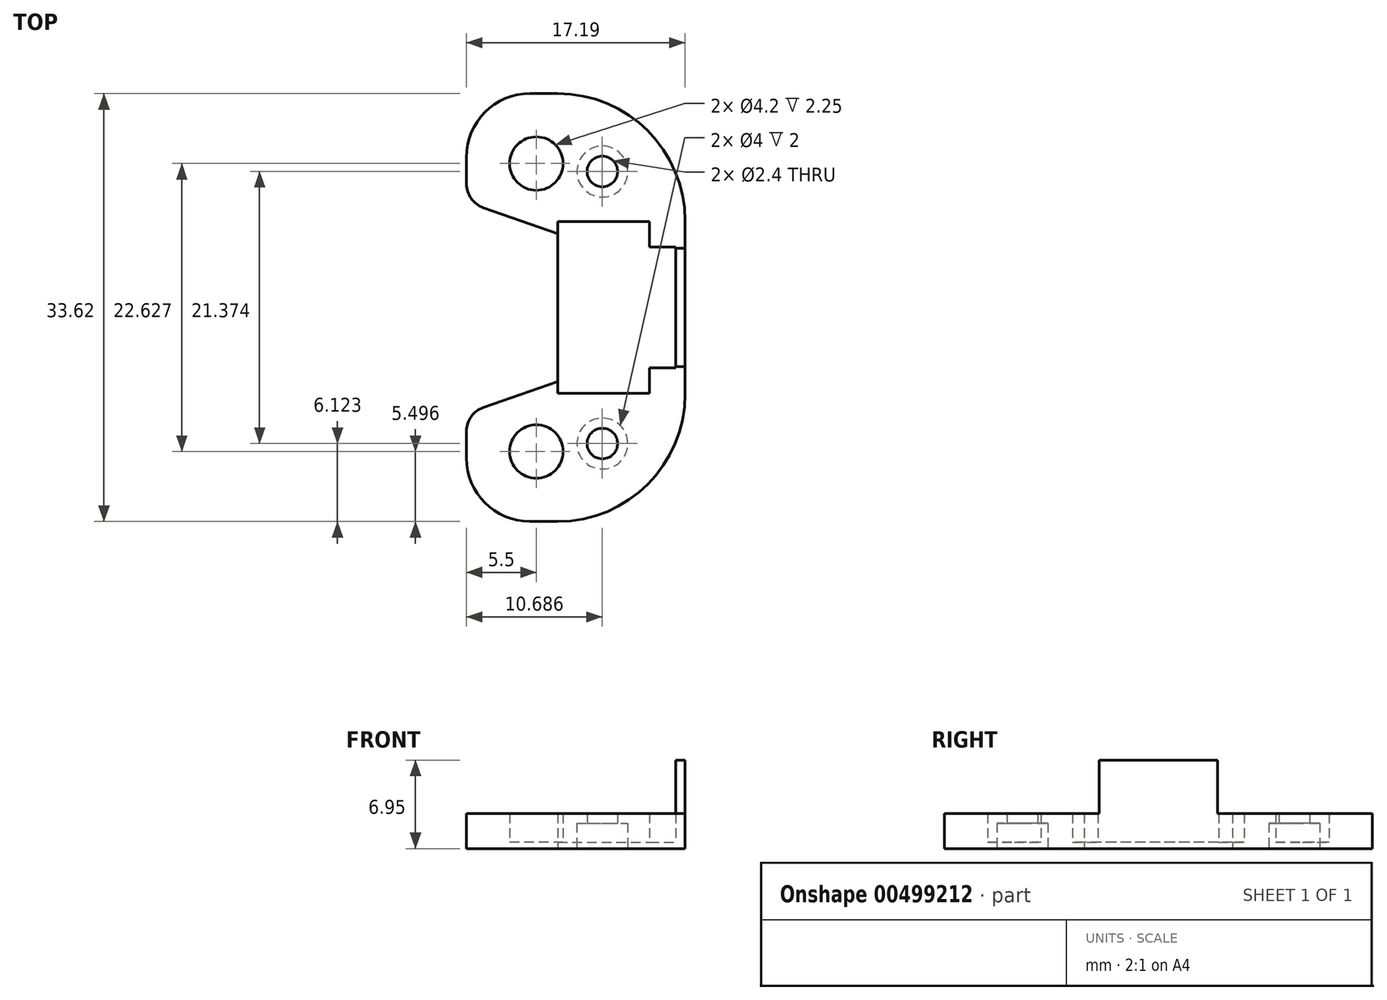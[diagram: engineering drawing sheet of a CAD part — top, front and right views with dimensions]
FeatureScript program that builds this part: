
annotation { "Feature Type Name" : "Feature", "Feature Type Description" : "" }
export const myFeature = defineFeature(function(context is Context, id is Id, definition is map)
    precondition{}
    {
        {
            var Q0;
            Q0=qCreatedBy(makeId("Top.planeOp"),FACE);
            var sketch = newSketch(context, id + "F0", { "sketchPlane" : qUnion([Q0])});
            skLineSegment(sketch, "E0.bottom", {"start": v(5.5, 16.81) * mm, "end": v(-0.5, 16.81) * mm});
            skLineSegment(sketch, "E0.top", {"start": v(5.5, 5.81) * mm, "end": v(-5.5, 5.81) * mm});
            skLineSegment(sketch, "E0.right", {"start": v(-5.5, 11.81) * mm, "end": v(-5.5, 5.81) * mm});
            skPoint(sketch, "E0.middle", {"position": v(0, 11.31) * mm});
            skLineSegment(sketch, "E1.bottom", {"start": v(5.5, -5.81) * mm, "end": v(-5.5, -5.81) * mm});
            skLineSegment(sketch, "E1.top", {"start": v(5.5, -16.81) * mm, "end": v(-0.5, -16.81) * mm});
            skLineSegment(sketch, "E1.right", {"start": v(-5.5, -5.81) * mm, "end": v(-5.5, -11.81) * mm});
            skPoint(sketch, "E1.middle", {"position": v(0, -11.31) * mm});
            skLineSegment(sketch, "E2", {"start": v(5.5, 16.81) * mm, "end": v(11.69, 16.81) * mm});
            skLineSegment(sketch, "E3", {"start": v(11.69, 16.81) * mm, "end": v(11.69, -16.81) * mm});
            skLineSegment(sketch, "E4", {"start": v(11.69, -16.81) * mm, "end": v(5.5, -16.81) * mm});
            skLineSegment(sketch, "E5", {"start": v(5.5, 5.81) * mm, "end": v(1.69, 5.81) * mm});
            skLineSegment(sketch, "E6", {"start": v(1.69, 5.81) * mm, "end": v(1.69, -5.81) * mm});
            skLineSegment(sketch, "E7", {"start": v(5.5, -5.81) * mm, "end": v(1.69, -5.81) * mm});
            skPoint(sketch, "E8", {"position": v(-11.31, 0) * mm});
            skLineSegment(sketch, "E9", {"start": v(1.69, -5.81) * mm, "end": v(-5.5, -8.31) * mm});
            skPoint(sketch, "E10.visualSharp", {"position": v(-5.5, -16.81) * mm});
            skArc(sketch, "E10.filletArc", {"start": v(-5.5, -11.81) * mm, "mid": v(-4.04, -15.35) * mm, "end": v(-0.5, -16.81) * mm});
            skPoint(sketch, "E11.visualSharp", {"position": v(-5.5, 16.81) * mm});
            skArc(sketch, "E11.filletArc", {"start": v(-0.5, 16.81) * mm, "mid": v(-4.04, 15.35) * mm, "end": v(-5.5, 11.81) * mm});
            skLineSegment(sketch, "E12", {"start": v(1.69, 5.81) * mm, "end": v(-5.5, 8.31) * mm});
            skCircle(sketch, "E13", {"center": v(0, -11.31) * mm, "radius": 2.1 * mm});
            skCircle(sketch, "E14", {"center": v(0, 11.31) * mm, "radius": 2.1 * mm});
            skSolve(sketch);
        }
        {
            var Q0;
            Q0=makeQuery(id+"F0.imprint","IMPRINT",FACE,{"disambiguationData":[TD([[makeQuery(id+"F0.imprint","IMPRINT",EDGE,{"derivedFrom":sQuery(id+"F0.wireOp",EDGE,"E0.bottom")}),1.0]])]});
            extrude(context, id + "F1", {"entities" : qUnion([Q0]), "depth" : 2.75 * mm});
        }
        {
            var Q0;
            Q0=makeQuery(id+"F1.opExtrude","SWEPT_FACE",FACE,{"disambiguationData":[OSD([sQuery(id+"F0.wireOp",EDGE,"E3")])]});
            var sketch = newSketch(context, id + "F2", { "sketchPlane" : qUnion([Q0])});
            skLineSegment(sketch, "E15.bottom", {"start": v(-6.75, 0.5) * mm, "end": v(6.75, 0.5) * mm});
            skLineSegment(sketch, "E15.top", {"start": v(-6.75, 2.75) * mm, "end": v(6.75, 2.75) * mm});
            skLineSegment(sketch, "E15.left", {"start": v(-6.75, 0.5) * mm, "end": v(-6.75, 2.75) * mm});
            skLineSegment(sketch, "E15.right", {"start": v(6.75, 0.5) * mm, "end": v(6.75, 2.75) * mm});
            skSolve(sketch);
        }
        {
            var Q0;
            Q0 = qSketchRegion(id + "F2", true);
            var Q1;
            Q1=makeQuery(id+"F1.opExtrude","SWEPT_FACE",FACE,{"disambiguationData":[OSD([sQuery(id+"F0.wireOp",EDGE,"E6")])]});
            extrude(context, id + "F3", {"entities" : qUnion([Q0]), "operationType" : NewBodyOperationType.REMOVE, "endBound" : BoundingType.UP_TO_SURFACE, "oppositeDirection" : true, "endBoundEntityFace" : qUnion([Q1]), "depth" : 25 * mm});
        }
        {
            var Q0;
            Q0=makeQuery(id+"F3.boolean.opBoolean","COPY",FACE,{"derivedFrom":makeQuery(id+"F3.opExtrude","SWEPT_FACE",FACE,{"disambiguationData":[OSD([sQuery(id+"F2.wireOp",EDGE,"E15.bottom")])]})});
            var sketch = newSketch(context, id + "F4", { "sketchPlane" : qUnion([Q0])});
            skLineSegment(sketch, "E16.bottom", {"start": v(11.69, -6.75) * mm, "end": v(8.89, -6.75) * mm});
            skLineSegment(sketch, "E16.top", {"start": v(11.69, 6.75) * mm, "end": v(8.89, 6.75) * mm});
            skLineSegment(sketch, "E16.left", {"start": v(11.69, -6.75) * mm, "end": v(11.69, -4.75) * mm});
            skLineSegment(sketch, "E16.right", {"start": v(8.89, -6.75) * mm, "end": v(8.89, -4.75) * mm});
            skLineSegment(sketch, "E17", {"start": v(8.89, -4.75) * mm, "end": v(11.69, -4.75) * mm});
            skLineSegment(sketch, "E18", {"start": v(8.89, 4.75) * mm, "end": v(11.69, 4.75) * mm});
            skLineSegment(sketch, "E19.trimOffspring", {"start": v(8.89, 4.75) * mm, "end": v(8.89, 6.75) * mm});
            skLineSegment(sketch, "E20.trimOffspring", {"start": v(11.69, 4.75) * mm, "end": v(11.69, 6.75) * mm});
            skSolve(sketch);
        }
        {
            var Q0;
            Q0 = qSketchRegion(id + "F4", true);
            var Q1;
            {var subQ0=sQuery(id+"F0.wireOp",EDGE,"E9");var subQ1=sQuery(id+"F0.wireOp",EDGE,"E3");var subQ2=sQuery(id+"F0.wireOp",EDGE,"E1.right");var subQ4=sQuery(id+"F0.wireOp",EDGE,"E4");var subQ5=sQuery(id+"F0.wireOp",EDGE,"E1.top");var subQ6=sQuery(id+"F0.wireOp",EDGE,"E10.filletArc");var subQ7=sQuery(id+"F0.wireOp",EDGE,"E13");Q1=makeQuery(id+"F3.boolean.opBoolean","SPLIT",FACE,{"disambiguationData":[TD([makeQuery(id+"F1.opExtrude","SWEPT_FACE",FACE,{"disambiguationData":[OSD([subQ2])]})])],"derivedFrom":makeQuery(id+"F1.opExtrude","CAP_FACE",FACE,{"disambiguationData":[OSD([sQuery(id+"F0.wireOp",EDGE,"E0.bottom"),sQuery(id+"F0.wireOp",EDGE,"E0.right"),subQ5,subQ2,sQuery(id+"F0.wireOp",EDGE,"E2"),subQ1,subQ4,sQuery(id+"F0.wireOp",EDGE,"E6"),subQ0,subQ6,sQuery(id+"F0.wireOp",EDGE,"E11.filletArc"),sQuery(id+"F0.wireOp",EDGE,"E12"),subQ7,sQuery(id+"F0.wireOp",EDGE,"E14")])],"isStart":false})});}
            extrude(context, id + "F5", {"entities" : qUnion([Q0]), "operationType" : NewBodyOperationType.ADD, "endBound" : BoundingType.UP_TO_SURFACE, "endBoundEntityFace" : qUnion([Q1]), "depth" : 25 * mm});
        }
        {
            var Q0;
            Q0=makeQuery(id+"F1.opExtrude","SWEPT_EDGE",EDGE,{"disambiguationData":[OSD([sQuery(id+"F0.wireOp",EDGE,"E3"),sQuery(id+"F0.wireOp",EDGE,"E4")])]});
            var Q1;
            Q1=makeQuery(id+"F1.opExtrude","SWEPT_EDGE",EDGE,{"disambiguationData":[OSD([sQuery(id+"F0.wireOp",EDGE,"E2"),sQuery(id+"F0.wireOp",EDGE,"E3")])]});
            fillet(context, id + "F6", {"entities" : qUnion([Q0, Q1]), "radius" : 10 * mm, "tangentPropagation" : true, "allowEdgeOverflow" : false});
        }
        {
            var Q0;
            Q0=makeQuery(id+"F1.opExtrude","SWEPT_EDGE",EDGE,{"disambiguationData":[OSD([sQuery(id+"F0.wireOp",EDGE,"E1.right"),sQuery(id+"F0.wireOp",EDGE,"E9")])]});
            var Q1;
            Q1=makeQuery(id+"F1.opExtrude","SWEPT_EDGE",EDGE,{"disambiguationData":[OSD([sQuery(id+"F0.wireOp",EDGE,"E0.right"),sQuery(id+"F0.wireOp",EDGE,"E12")])]});
            fillet(context, id + "F7", {"entities" : qUnion([Q0, Q1]), "radius" : 2 * mm, "tangentPropagation" : true, "allowEdgeOverflow" : false});
        }
        {
            var Q0;
            Q0=makeQuery(id+"F1.opExtrude","CAP_FACE",FACE,{"disambiguationData":[OSD([sQuery(id+"F0.wireOp",EDGE,"E0.bottom"),sQuery(id+"F0.wireOp",EDGE,"E0.right"),sQuery(id+"F0.wireOp",EDGE,"E1.top"),sQuery(id+"F0.wireOp",EDGE,"E1.right"),sQuery(id+"F0.wireOp",EDGE,"E2"),sQuery(id+"F0.wireOp",EDGE,"E3"),sQuery(id+"F0.wireOp",EDGE,"E4"),sQuery(id+"F0.wireOp",EDGE,"E6"),sQuery(id+"F0.wireOp",EDGE,"E9"),sQuery(id+"F0.wireOp",EDGE,"E10.filletArc"),sQuery(id+"F0.wireOp",EDGE,"E11.filletArc"),sQuery(id+"F0.wireOp",EDGE,"E12"),sQuery(id+"F0.wireOp",EDGE,"E13"),sQuery(id+"F0.wireOp",EDGE,"E14")])],"isStart":true});
            var sketch = newSketch(context, id + "F8", { "sketchPlane" : qUnion([Q0])});
            skCircle(sketch, "E21", {"center": v(5.19, -10.69) * mm, "radius": 2 * mm});
            skCircle(sketch, "E22", {"center": v(5.19, 10.69) * mm, "radius": 2 * mm});
            skSolve(sketch);
        }
        {
            var Q0;
            Q0 = qSketchRegion(id + "F8", true);
            extrude(context, id + "F9", {"entities" : qUnion([Q0]), "operationType" : NewBodyOperationType.REMOVE, "oppositeDirection" : true, "depth" : 2 * mm});
        }
        {
            var Q0;
            Q0=makeQuery(id+"F9.boolean.opBoolean","COPY",FACE,{"derivedFrom":makeQuery(id+"F9.opExtrude","CAP_FACE",FACE,{"disambiguationData":[OSD([sQuery(id+"F8.wireOp",EDGE,"E21")])],"isStart":false})});
            var sketch = newSketch(context, id + "F10", { "sketchPlane" : qUnion([Q0])});
            skCircle(sketch, "E23", {"center": v(5.19, -10.69) * mm, "radius": 1.2 * mm});
            skSolve(sketch);
        }
        {
            var Q0;
            Q0=makeQuery(id+"F9.boolean.opBoolean","COPY",FACE,{"derivedFrom":makeQuery(id+"F9.opExtrude","CAP_FACE",FACE,{"disambiguationData":[OSD([sQuery(id+"F8.wireOp",EDGE,"E22")])],"isStart":false})});
            var sketch = newSketch(context, id + "F11", { "sketchPlane" : qUnion([Q0])});
            skCircle(sketch, "E24", {"center": v(5.19, 10.69) * mm, "radius": 1.2 * mm});
            skSolve(sketch);
        }
        {
            var Q0;
            Q0 = qSketchRegion(id + "F10", true);
            var Q1;
            Q1 = qSketchRegion(id + "F11", true);
            var Q2;
            {var subQ0=sQuery(id+"F0.wireOp",EDGE,"E11.filletArc");var subQ1=sQuery(id+"F0.wireOp",EDGE,"E3");var subQ3=sQuery(id+"F0.wireOp",EDGE,"E0.right");var subQ4=sQuery(id+"F0.wireOp",EDGE,"E2");var subQ5=sQuery(id+"F0.wireOp",EDGE,"E0.bottom");var subQ6=sQuery(id+"F0.wireOp",EDGE,"E14");var subQ7=sQuery(id+"F0.wireOp",EDGE,"E12");Q2=makeQuery(id+"F5.boolean.opBoolean","MERGE",FACE,{"derivedFrom":[makeQuery(id+"F3.boolean.opBoolean","SPLIT",FACE,{"disambiguationData":[TD([makeQuery(id+"F1.opExtrude","SWEPT_FACE",FACE,{"disambiguationData":[OSD([subQ3])]})])],"derivedFrom":makeQuery(id+"F1.opExtrude","CAP_FACE",FACE,{"disambiguationData":[OSD([subQ5,subQ3,sQuery(id+"F0.wireOp",EDGE,"E1.top"),sQuery(id+"F0.wireOp",EDGE,"E1.right"),subQ4,subQ1,sQuery(id+"F0.wireOp",EDGE,"E4"),sQuery(id+"F0.wireOp",EDGE,"E6"),sQuery(id+"F0.wireOp",EDGE,"E9"),sQuery(id+"F0.wireOp",EDGE,"E10.filletArc"),subQ0,subQ7,sQuery(id+"F0.wireOp",EDGE,"E13"),subQ6])],"isStart":false})}),makeQuery(id+"F5.opExtrude","CAP_FACE",FACE,{"disambiguationData":[OSD([sQuery(id+"F4.wireOp",EDGE,"E16.top"),sQuery(id+"F4.wireOp",EDGE,"E18"),sQuery(id+"F4.wireOp",EDGE,"E19.trimOffspring"),sQuery(id+"F4.wireOp",EDGE,"E20.trimOffspring")])],"isStart":false})]});}
            extrude(context, id + "F12", {"entities" : qUnion([Q0, Q1]), "operationType" : NewBodyOperationType.REMOVE, "endBound" : BoundingType.UP_TO_SURFACE, "oppositeDirection" : true, "endBoundEntityFace" : qUnion([Q2]), "depth" : 25 * mm});
        }
        {
            var Q0;
            Q0=makeQuery(id+"F3.boolean.opBoolean","COPY",FACE,{"derivedFrom":makeQuery(id+"F3.opExtrude","SWEPT_FACE",FACE,{"disambiguationData":[OSD([sQuery(id+"F2.wireOp",EDGE,"E15.bottom")])]})});
            var sketch = newSketch(context, id + "F13", { "sketchPlane" : qUnion([Q0])});
            skLineSegment(sketch, "E25.bottom", {"start": v(11.69, 4.75) * mm, "end": v(10.94, 4.75) * mm});
            skLineSegment(sketch, "E25.top", {"start": v(11.69, -4.75) * mm, "end": v(10.94, -4.75) * mm});
            skLineSegment(sketch, "E25.left", {"start": v(11.69, 4.75) * mm, "end": v(11.69, -4.75) * mm});
            skLineSegment(sketch, "E25.right", {"start": v(10.94, 4.75) * mm, "end": v(10.94, -4.75) * mm});
            skSolve(sketch);
        }
        {
            var Q0;
            Q0 = qSketchRegion(id + "F13", true);
            var Q1;
            {var subQ0=sQuery(id+"F0.wireOp",EDGE,"E11.filletArc");var subQ1=sQuery(id+"F0.wireOp",EDGE,"E3");var subQ3=sQuery(id+"F0.wireOp",EDGE,"E0.right");var subQ4=sQuery(id+"F0.wireOp",EDGE,"E2");var subQ5=sQuery(id+"F0.wireOp",EDGE,"E0.bottom");var subQ6=sQuery(id+"F0.wireOp",EDGE,"E14");var subQ7=sQuery(id+"F0.wireOp",EDGE,"E12");Q1=makeQuery(id+"F5.boolean.opBoolean","MERGE",FACE,{"derivedFrom":[makeQuery(id+"F3.boolean.opBoolean","SPLIT",FACE,{"disambiguationData":[TD([makeQuery(id+"F1.opExtrude","SWEPT_FACE",FACE,{"disambiguationData":[OSD([subQ3])]})])],"derivedFrom":makeQuery(id+"F1.opExtrude","CAP_FACE",FACE,{"disambiguationData":[OSD([subQ5,subQ3,sQuery(id+"F0.wireOp",EDGE,"E1.top"),sQuery(id+"F0.wireOp",EDGE,"E1.right"),subQ4,subQ1,sQuery(id+"F0.wireOp",EDGE,"E4"),sQuery(id+"F0.wireOp",EDGE,"E6"),sQuery(id+"F0.wireOp",EDGE,"E9"),sQuery(id+"F0.wireOp",EDGE,"E10.filletArc"),subQ0,subQ7,sQuery(id+"F0.wireOp",EDGE,"E13"),subQ6])],"isStart":false})}),makeQuery(id+"F5.opExtrude","CAP_FACE",FACE,{"disambiguationData":[OSD([sQuery(id+"F4.wireOp",EDGE,"E16.top"),sQuery(id+"F4.wireOp",EDGE,"E18"),sQuery(id+"F4.wireOp",EDGE,"E19.trimOffspring"),sQuery(id+"F4.wireOp",EDGE,"E20.trimOffspring")])],"isStart":false})]});}
            extrude(context, id + "F14", {"entities" : qUnion([Q0]), "operationType" : NewBodyOperationType.ADD, "endBound" : BoundingType.UP_TO_SURFACE, "endBoundEntityFace" : qUnion([Q1]), "depth" : 4 * mm});
        }
        {
            var Q0;
            {var subQ0=sQuery(id+"F0.wireOp",EDGE,"E9");var subQ1=sQuery(id+"F0.wireOp",EDGE,"E3");var subQ3=sQuery(id+"F0.wireOp",EDGE,"E1.right");var subQ5=sQuery(id+"F0.wireOp",EDGE,"E4");var subQ6=sQuery(id+"F0.wireOp",EDGE,"E1.top");var subQ7=sQuery(id+"F0.wireOp",EDGE,"E10.filletArc");var subQ8=sQuery(id+"F0.wireOp",EDGE,"E13");var subQ11=sQuery(id+"F0.wireOp",EDGE,"E14");var subQ12=sQuery(id+"F0.wireOp",EDGE,"E12");var subQ13=sQuery(id+"F0.wireOp",EDGE,"E11.filletArc");var subQ14=sQuery(id+"F0.wireOp",EDGE,"E2");var subQ15=sQuery(id+"F0.wireOp",EDGE,"E0.right");var subQ16=sQuery(id+"F0.wireOp",EDGE,"E0.bottom");var subQ17=makeQuery(id+"F1.opExtrude","CAP_FACE",FACE,{"disambiguationData":[OSD([subQ16,subQ15,subQ6,subQ3,subQ14,subQ1,subQ5,sQuery(id+"F0.wireOp",EDGE,"E6"),subQ0,subQ7,subQ13,subQ12,subQ8,subQ11])],"isStart":false});Q0=makeQuery(id+"F14.boolean.opBoolean","MERGE",FACE,{"derivedFrom":[makeQuery(id+"F5.boolean.opBoolean","MERGE",FACE,{"derivedFrom":[makeQuery(id+"F3.boolean.opBoolean","SPLIT",FACE,{"disambiguationData":[TD([makeQuery(id+"F1.opExtrude","SWEPT_FACE",FACE,{"disambiguationData":[OSD([subQ15])]})])],"derivedFrom":subQ17}),makeQuery(id+"F5.opExtrude","CAP_FACE",FACE,{"disambiguationData":[OSD([sQuery(id+"F4.wireOp",EDGE,"E16.top"),sQuery(id+"F4.wireOp",EDGE,"E18"),sQuery(id+"F4.wireOp",EDGE,"E19.trimOffspring"),sQuery(id+"F4.wireOp",EDGE,"E20.trimOffspring")])],"isStart":false})]}),makeQuery(id+"F5.boolean.opBoolean","MERGE",FACE,{"derivedFrom":[makeQuery(id+"F3.boolean.opBoolean","SPLIT",FACE,{"disambiguationData":[TD([makeQuery(id+"F1.opExtrude","SWEPT_FACE",FACE,{"disambiguationData":[OSD([subQ3])]})])],"derivedFrom":subQ17}),makeQuery(id+"F5.opExtrude","CAP_FACE",FACE,{"disambiguationData":[OSD([sQuery(id+"F4.wireOp",EDGE,"E16.bottom"),sQuery(id+"F4.wireOp",EDGE,"E16.left"),sQuery(id+"F4.wireOp",EDGE,"E16.right"),sQuery(id+"F4.wireOp",EDGE,"E17")])],"isStart":false})]}),makeQuery(id+"F14.opExtrude","CAP_FACE",FACE,{"disambiguationData":[OSD([sQuery(id+"F13.wireOp",EDGE,"E25.bottom"),sQuery(id+"F13.wireOp",EDGE,"E25.top"),sQuery(id+"F13.wireOp",EDGE,"E25.left"),sQuery(id+"F13.wireOp",EDGE,"E25.right")])],"isStart":false})]});}
            var sketch = newSketch(context, id + "F15", { "sketchPlane" : qUnion([Q0])});
            skLineSegment(sketch, "E26.bottom", {"start": v(10.94, -4.75) * mm, "end": v(11.69, -4.75) * mm});
            skLineSegment(sketch, "E26.top", {"start": v(10.94, 4.75) * mm, "end": v(11.69, 4.75) * mm});
            skLineSegment(sketch, "E26.left", {"start": v(10.94, -4.75) * mm, "end": v(10.94, 4.75) * mm});
            skLineSegment(sketch, "E26.right", {"start": v(11.69, -4.75) * mm, "end": v(11.69, 4.75) * mm});
            skSolve(sketch);
        }
        {
            var Q0;
            Q0 = qSketchRegion(id + "F15", true);
            extrude(context, id + "F16", {"entities" : qUnion([Q0]), "operationType" : NewBodyOperationType.ADD, "depth" : 4.2 * mm});
        }
        {
            var Q0;
            Q0=makeQuery(id+"F1.opExtrude","CAP_FACE",FACE,{"disambiguationData":[OSD([sQuery(id+"F0.wireOp",EDGE,"E0.bottom"),sQuery(id+"F0.wireOp",EDGE,"E0.right"),sQuery(id+"F0.wireOp",EDGE,"E1.top"),sQuery(id+"F0.wireOp",EDGE,"E1.right"),sQuery(id+"F0.wireOp",EDGE,"E2"),sQuery(id+"F0.wireOp",EDGE,"E3"),sQuery(id+"F0.wireOp",EDGE,"E4"),sQuery(id+"F0.wireOp",EDGE,"E6"),sQuery(id+"F0.wireOp",EDGE,"E9"),sQuery(id+"F0.wireOp",EDGE,"E10.filletArc"),sQuery(id+"F0.wireOp",EDGE,"E11.filletArc"),sQuery(id+"F0.wireOp",EDGE,"E12"),sQuery(id+"F0.wireOp",EDGE,"E13"),sQuery(id+"F0.wireOp",EDGE,"E14")])],"isStart":true});
            var sketch = newSketch(context, id + "F17", { "sketchPlane" : qUnion([Q0])});
            skCircle(sketch, "E27", {"center": v(0, 11.31) * mm, "radius": 2.1 * mm});
            skCircle(sketch, "E28", {"center": v(0, -11.31) * mm, "radius": 2.1 * mm});
            skSolve(sketch);
        }
        {
            var Q0;
            Q0 = qSketchRegion(id + "F17", true);
            extrude(context, id + "F18", {"entities" : qUnion([Q0]), "operationType" : NewBodyOperationType.ADD, "oppositeDirection" : true, "depth" : 0.5 * mm});
        }
        {
            var Q0;
            Q0=makeQuery(id+"F16.opExtrude","CAP_FACE",FACE,{"disambiguationData":[OSD([sQuery(id+"F15.wireOp",EDGE,"E26.bottom"),sQuery(id+"F15.wireOp",EDGE,"E26.top"),sQuery(id+"F15.wireOp",EDGE,"E26.left"),sQuery(id+"F15.wireOp",EDGE,"E26.right")])],"isStart":false});
            var sketch = newSketch(context, id + "F19", { "sketchPlane" : qUnion([Q0])});
            skLineSegment(sketch, "E29.bottom", {"start": v(10.94, 4.75) * mm, "end": v(11.69, 4.75) * mm});
            skLineSegment(sketch, "E29.top", {"start": v(10.94, 4.65) * mm, "end": v(11.69, 4.65) * mm});
            skLineSegment(sketch, "E29.left", {"start": v(10.94, 4.75) * mm, "end": v(10.94, 4.65) * mm});
            skLineSegment(sketch, "E29.right", {"start": v(11.69, 4.75) * mm, "end": v(11.69, 4.65) * mm});
            skLineSegment(sketch, "E30.bottom", {"start": v(10.94, -4.75) * mm, "end": v(11.69, -4.75) * mm});
            skLineSegment(sketch, "E30.top", {"start": v(10.94, -4.65) * mm, "end": v(11.69, -4.65) * mm});
            skLineSegment(sketch, "E30.left", {"start": v(10.94, -4.75) * mm, "end": v(10.94, -4.65) * mm});
            skLineSegment(sketch, "E30.right", {"start": v(11.69, -4.75) * mm, "end": v(11.69, -4.65) * mm});
            skSolve(sketch);
        }
        {
            var Q0;
            Q0 = qSketchRegion(id + "F19", true);
            var Q1;
            {var subQ0=sQuery(id+"F4.wireOp",EDGE,"E16.right");var subQ1=sQuery(id+"F4.wireOp",EDGE,"E16.left");var subQ3=sQuery(id+"F0.wireOp",EDGE,"E14");var subQ4=sQuery(id+"F0.wireOp",EDGE,"E13");var subQ5=sQuery(id+"F0.wireOp",EDGE,"E12");var subQ6=sQuery(id+"F0.wireOp",EDGE,"E11.filletArc");var subQ7=sQuery(id+"F0.wireOp",EDGE,"E10.filletArc");var subQ8=sQuery(id+"F0.wireOp",EDGE,"E9");var subQ9=sQuery(id+"F0.wireOp",EDGE,"E6");var subQ10=sQuery(id+"F0.wireOp",EDGE,"E4");var subQ11=sQuery(id+"F0.wireOp",EDGE,"E3");var subQ12=sQuery(id+"F0.wireOp",EDGE,"E2");var subQ13=sQuery(id+"F0.wireOp",EDGE,"E1.right");var subQ14=sQuery(id+"F0.wireOp",EDGE,"E1.top");var subQ15=sQuery(id+"F0.wireOp",EDGE,"E0.right");var subQ16=sQuery(id+"F0.wireOp",EDGE,"E0.bottom");var subQ17=makeQuery(id+"F1.opExtrude","CAP_FACE",FACE,{"disambiguationData":[OSD([subQ16,subQ15,subQ14,subQ13,subQ12,subQ11,subQ10,subQ9,subQ8,subQ7,subQ6,subQ5,subQ4,subQ3])],"isStart":false});var subQ26=sQuery(id+"F13.wireOp",EDGE,"E25.left");var subQ27=makeQuery(id+"F1.opExtrude","SWEPT_FACE",FACE,{"disambiguationData":[OSD([subQ13])]});var subQ28=sQuery(id+"F4.wireOp",EDGE,"E20.trimOffspring");var subQ29=sQuery(id+"F13.wireOp",EDGE,"E25.right");var subQ31=sQuery(id+"F4.wireOp",EDGE,"E17");Q1=makeQuery(id+"F16.boolean.opBoolean","SPLIT",FACE,{"disambiguationData":[TD([subQ27])],"derivedFrom":makeQuery(id+"F14.boolean.opBoolean","MERGE",FACE,{"derivedFrom":[makeQuery(id+"F5.boolean.opBoolean","MERGE",FACE,{"derivedFrom":[makeQuery(id+"F3.boolean.opBoolean","SPLIT",FACE,{"disambiguationData":[TD([makeQuery(id+"F1.opExtrude","SWEPT_FACE",FACE,{"disambiguationData":[OSD([subQ15])]})])],"derivedFrom":subQ17}),makeQuery(id+"F5.opExtrude","CAP_FACE",FACE,{"disambiguationData":[OSD([sQuery(id+"F4.wireOp",EDGE,"E16.top"),sQuery(id+"F4.wireOp",EDGE,"E18"),sQuery(id+"F4.wireOp",EDGE,"E19.trimOffspring"),subQ28])],"isStart":false})]}),makeQuery(id+"F5.boolean.opBoolean","MERGE",FACE,{"derivedFrom":[makeQuery(id+"F3.boolean.opBoolean","SPLIT",FACE,{"disambiguationData":[TD([subQ27])],"derivedFrom":subQ17}),makeQuery(id+"F5.opExtrude","CAP_FACE",FACE,{"disambiguationData":[OSD([sQuery(id+"F4.wireOp",EDGE,"E16.bottom"),subQ1,subQ0,subQ31])],"isStart":false})]}),makeQuery(id+"F14.opExtrude","CAP_FACE",FACE,{"disambiguationData":[OSD([sQuery(id+"F13.wireOp",EDGE,"E25.bottom"),sQuery(id+"F13.wireOp",EDGE,"E25.top"),subQ26,subQ29])],"isStart":false})]})});}
            extrude(context, id + "F20", {"entities" : qUnion([Q0]), "operationType" : NewBodyOperationType.REMOVE, "endBound" : BoundingType.UP_TO_SURFACE, "oppositeDirection" : true, "endBoundEntityFace" : qUnion([Q1]), "depth" : 25 * mm});
        }
    });
